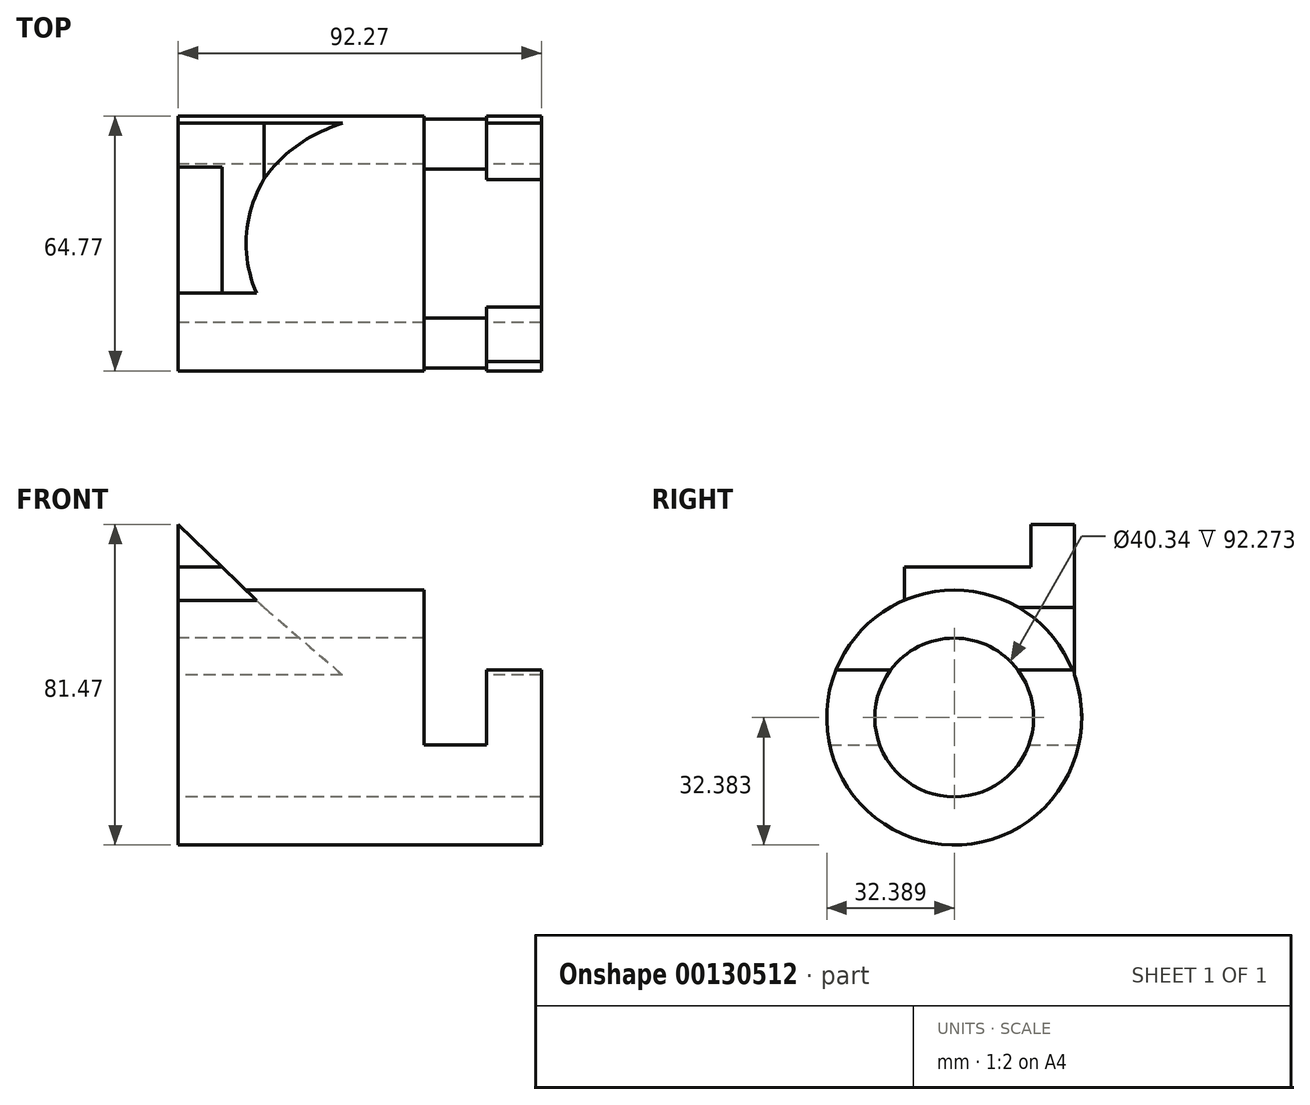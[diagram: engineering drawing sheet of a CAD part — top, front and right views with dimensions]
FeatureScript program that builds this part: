
annotation { "Feature Type Name" : "Feature", "Feature Type Description" : "" }
export const myFeature = defineFeature(function(context is Context, id is Id, definition is map)
    precondition{}
    {
        {
            var Q0;
            Q0=qCreatedBy(makeId("Front.planeOp"),FACE);
            var sketch = newSketch(context, id + "F0", { "sketchPlane" : qUnion([Q0])});
            skLineSegment(sketch, "E0", {"start": v(0, 0) * mm, "end": v(0, 90.45) * mm});
            skLineSegment(sketch, "E1", {"start": v(0, 90.45) * mm, "end": v(21.83, 69.29) * mm});
            skLineSegment(sketch, "E2", {"start": v(21.83, 69.29) * mm, "end": v(62.5, 69.29) * mm, "construction": true});
            skLineSegment(sketch, "E3", {"start": v(62.5, 69.29) * mm, "end": v(62.5, 34.36) * mm, "construction": true});
            skLineSegment(sketch, "E4", {"start": v(62.5, 34.36) * mm, "end": v(78.38, 34.36) * mm});
            skLineSegment(sketch, "E5", {"start": v(78.38, 34.36) * mm, "end": v(78.38, 53.41) * mm});
            skLineSegment(sketch, "E6", {"start": v(78.38, 53.41) * mm, "end": v(92.27, 53.41) * mm});
            skLineSegment(sketch, "E7", {"start": v(92.27, 53.41) * mm, "end": v(92.27, 0) * mm});
            skLineSegment(sketch, "E8", {"start": v(92.27, 0) * mm, "end": v(0, 0) * mm});
            skLineSegment(sketch, "E9", {"start": v(21.83, 69.29) * mm, "end": v(21.83, 0) * mm});
            skLineSegment(sketch, "E10", {"start": v(21.83, 69.29) * mm, "end": v(62.5, 34.36) * mm});
            skSolve(sketch);
        }
        {
            var Q0;
            Q0 = qSketchRegion(id + "F0", true);
            extrude(context, id + "F1", {"entities" : qUnion([Q0]), "oppositeDirection" : true, "depth" : 43.18 * mm});
        }
        {
            var Q0;
            Q0=qCreatedBy(makeId("Right.planeOp"),FACE);
            var sketch = newSketch(context, id + "F2", { "sketchPlane" : qUnion([Q0])});
            skCircle(sketch, "E11", {"center": v(12.67, 41.36) * mm, "radius": 20.17 * mm, "construction": true});
            skLineSegment(sketch, "E12.bottom", {"start": v(0, 79.66) * mm, "end": v(32.1, 79.66) * mm});
            skLineSegment(sketch, "E12.top", {"start": v(0, 90.45) * mm, "end": v(32.1, 90.45) * mm});
            skLineSegment(sketch, "E12.left", {"start": v(0, 79.66) * mm, "end": v(0, 90.45) * mm});
            skLineSegment(sketch, "E12.right", {"start": v(32.1, 79.66) * mm, "end": v(32.1, 90.45) * mm});
            skLineSegment(sketch, "E13", {"start": v(-17.4, 0) * mm, "end": v(43.18, 0) * mm});
            skLineSegment(sketch, "E14", {"start": v(43.18, 0) * mm, "end": v(43.18, 30.5) * mm});
            skLineSegment(sketch, "E15", {"start": v(-17.4, 0) * mm, "end": v(-17.4, 29.31) * mm});
            skArc(sketch, "E16", {"start": v(43.18, 30.5) * mm, "mid": v(13.3, 8.98) * mm, "end": v(-17.4, 29.31) * mm});
            skSolve(sketch);
        }
        {
            var Q0;
            Q0=qCreatedBy(makeId("Right.planeOp"),FACE);
            var sketch = newSketch(context, id + "F3", { "sketchPlane" : qUnion([Q0])});
            skCircle(sketch, "E17", {"center": v(12.67, 41.36) * mm, "radius": 32.39 * mm});
            skSolve(sketch);
        }
        {
            var Q0;
            Q0 = qSketchRegion(id + "F3", true);
            var Q1;
            Q1=makeQuery(id+"F1.opExtrude","SWEPT_FACE",FACE,{"disambiguationData":[OSD([sQuery(id+"F0.wireOp",EDGE,"E7")])]});
            extrude(context, id + "F4", {"entities" : qUnion([Q0]), "operationType" : NewBodyOperationType.ADD, "endBound" : BoundingType.UP_TO_SURFACE, "endBoundEntityFace" : qUnion([Q1]), "depth" : 62.5 * mm});
        }
        {
            var Q0;
            Q0 = qSketchRegion(id + "F2", true);
            var Q1;
            Q1=makeQuery(id+"F1.opExtrude","SWEPT_FACE",FACE,{"disambiguationData":[OSD([sQuery(id+"F0.wireOp",EDGE,"E3")])]});
            extrude(context, id + "F5", {"entities" : qUnion([Q0]), "operationType" : NewBodyOperationType.REMOVE, "endBound" : BoundingType.THROUGH_ALL, "endBoundEntityFace" : qUnion([Q1]), "depth" : 25.4 * mm});
        }
        {
            var Q0;
            Q0=qCreatedBy(makeId("Front.planeOp"),FACE);
            var sketch = newSketch(context, id + "F6", { "sketchPlane" : qUnion([Q0])});
            skLineSegment(sketch, "E18.bottom", {"start": v(62.5, 34.36) * mm, "end": v(78.38, 34.36) * mm});
            skLineSegment(sketch, "E18.top", {"start": v(62.5, 77.37) * mm, "end": v(78.38, 77.37) * mm});
            skLineSegment(sketch, "E18.left", {"start": v(62.5, 34.36) * mm, "end": v(62.5, 77.37) * mm});
            skLineSegment(sketch, "E18.right", {"start": v(78.38, 34.36) * mm, "end": v(78.38, 77.37) * mm});
            skSolve(sketch);
        }
        {
            var Q0;
            Q0 = qSketchRegion(id + "F6", true);
            var Q1;
            Q1=makeQuery(id+"F1.opExtrude","SWEPT_BODY",BODY,{"disambiguationData":[OSD([sQuery(id+"F0.wireOp",EDGE,"E0"),sQuery(id+"F0.wireOp",EDGE,"E1"),sQuery(id+"F0.wireOp",EDGE,"E2"),sQuery(id+"F0.wireOp",EDGE,"E3"),sQuery(id+"F0.wireOp",EDGE,"E4"),sQuery(id+"F0.wireOp",EDGE,"E5"),sQuery(id+"F0.wireOp",EDGE,"E6"),sQuery(id+"F0.wireOp",EDGE,"E7"),sQuery(id+"F0.wireOp",EDGE,"E8")])]});
            extrude(context, id + "F7", {"entities" : qUnion([Q0]), "operationType" : NewBodyOperationType.REMOVE, "endBound" : BoundingType.THROUGH_ALL, "depth" : 25.4 * mm, "hasSecondDirection" : true, "secondDirectionBound" : SecondDirectionBoundingType.UP_TO_BODY, "secondDirectionOppositeDirection" : true, "secondDirectionBoundEntityBody" : qUnion([Q1]), "secondDirectionDepth" : 25.4 * mm});
        }
        {
            var Q0;
            Q0=qCreatedBy(makeId("Right.planeOp"),FACE);
            var sketch = newSketch(context, id + "F8", { "sketchPlane" : qUnion([Q0])});
            skLineSegment(sketch, "E19", {"start": v(0, 53.41) * mm, "end": v(-17.4, 53.41) * mm});
            skLineSegment(sketch, "E20", {"start": v(43.18, 53.41) * mm, "end": v(0, 53.41) * mm});
            skLineSegment(sketch, "E21.bottom", {"start": v(-17.4, 53.41) * mm, "end": v(42.84, 53.41) * mm});
            skLineSegment(sketch, "E21.top", {"start": v(-17.4, 80.15) * mm, "end": v(42.84, 80.15) * mm});
            skLineSegment(sketch, "E21.left", {"start": v(-17.4, 53.41) * mm, "end": v(-17.4, 80.15) * mm});
            skLineSegment(sketch, "E21.right", {"start": v(42.84, 53.41) * mm, "end": v(42.84, 80.15) * mm});
            skSolve(sketch);
        }
        {
            var Q0;
            Q0 = qSketchRegion(id + "F8", true);
            var Q1;
            {var subQ0=sQuery(id+"F0.wireOp",EDGE,"E7");Q1=makeQuery(id+"F4.boolean.opBoolean","MERGE",FACE,{"derivedFrom":[makeQuery(id+"F1.opExtrude","SWEPT_FACE",FACE,{"disambiguationData":[OSD([subQ0])]}),makeQuery(id+"F4.opExtrude","CAP_FACE",FACE,{"disambiguationData":[OSD([subQ0])],"isStart":false})]});}
            var Q2;
            Q2=makeQuery(id+"F1.opExtrude","SWEPT_FACE",FACE,{"disambiguationData":[OSD([sQuery(id+"F0.wireOp",EDGE,"E5")])]});
            extrude(context, id + "F9", {"entities" : qUnion([Q0]), "operationType" : NewBodyOperationType.REMOVE, "endBound" : BoundingType.UP_TO_SURFACE, "endBoundEntityFace" : qUnion([Q1]), "depth" : 25.4 * mm, "hasSecondDirection" : true, "secondDirectionOppositeDirection" : false, "secondDirectionBoundEntityFace" : qUnion([Q2]), "secondDirectionDepth" : 78.23 * mm});
        }
        {
            var Q0;
            Q0=qCreatedBy(makeId("Right.planeOp"),FACE);
            var sketch = newSketch(context, id + "F10", { "sketchPlane" : qUnion([Q0])});
            skCircle(sketch, "E22", {"center": v(12.67, 41.36) * mm, "radius": 20.17 * mm});
            skSolve(sketch);
        }
        {
            var Q0;
            Q0 = qSketchRegion(id + "F10", true);
            extrude(context, id + "F11", {"entities" : qUnion([Q0]), "operationType" : NewBodyOperationType.REMOVE, "endBound" : BoundingType.THROUGH_ALL, "depth" : 25.4 * mm});
        }
    });
